FCSTD DOCUMENT  (FreeCAD 1.0R39319 (Git))
Label: caixa-chao
License: All rights reserved
LicenseURL: https://en.wikipedia.org/wiki/All_rights_reserved
objects: Part::Feature×1, Sketcher::SketchObject×1, PartDesign::Body×1
note: 4 computed .brp shape members not serialized (recipe doc carries the construction recipe); baked Part::Feature solids carry a one-line shape summary decoded from their .brp

FEATURE [Part::Feature] path46
  shape: bbox 266.2 x 266.2 x 2e-07 mm, 0 faces, 0 solids (baked)
FEATURE [Sketcher::SketchObject] Sketch
  ArcFitTolerance = 1e-06
  AttachmentSupport = -> [XY_Plane]
  FullyConstrained = true
  MakeInternals = false
  MapMode = 5
  sketch-geometry (28):
    g0: Circle CenterX=8 CenterY=-27.81 CenterZ=0 NormalX=0 NormalY=0 NormalZ=1 AngleXU=0 Radius=2
    g1: Circle CenterX=100.71 CenterY=-27.81 CenterZ=0 NormalX=0 NormalY=0 NormalZ=1 AngleXU=0 Radius=2
    g2: Circle CenterX=100.71 CenterY=-121.79 CenterZ=0 NormalX=0 NormalY=0 NormalZ=1 AngleXU=0 Radius=2
    g3: Circle CenterX=8 CenterY=-78.61 CenterZ=0 NormalX=0 NormalY=0 NormalZ=1 AngleXU=0 Radius=2
    g4: Circle CenterX=100.71 CenterY=-149.41 CenterZ=0 NormalX=0 NormalY=0 NormalZ=1 AngleXU=0 Radius=2
    g5: Circle CenterX=100.71 CenterY=-243.39 CenterZ=0 NormalX=0 NormalY=0 NormalZ=1 AngleXU=0 Radius=2
    g6: Circle CenterX=8 CenterY=-149.41 CenterZ=0 NormalX=0 NormalY=0 NormalZ=1 AngleXU=0 Radius=2
    g7: Circle CenterX=8 CenterY=-200.21 CenterZ=0 NormalX=0 NormalY=0 NormalZ=1 AngleXU=0 Radius=2
    g8: Circle CenterX=150.71 CenterY=-27.81 CenterZ=0 NormalX=0 NormalY=0 NormalZ=1 AngleXU=0 Radius=2
    g9: Circle CenterX=189.21 CenterY=-27.81 CenterZ=0 NormalX=0 NormalY=0 NormalZ=1 AngleXU=0 Radius=2
    g10: Circle CenterX=150.71 CenterY=-48.41 CenterZ=0 NormalX=0 NormalY=0 NormalZ=1 AngleXU=0 Radius=2
    g11: Circle CenterX=189.21 CenterY=-48.41 CenterZ=0 NormalX=0 NormalY=0 NormalZ=1 AngleXU=0 Radius=2
    g12: Circle CenterX=150.71 CenterY=-68.41 CenterZ=0 NormalX=0 NormalY=0 NormalZ=1 AngleXU=0 Radius=2
    g13: Circle CenterX=189.21 CenterY=-68.41 CenterZ=0 NormalX=0 NormalY=0 NormalZ=1 AngleXU=0 Radius=2
    g14: Circle CenterX=189.21 CenterY=-89.01 CenterZ=0 NormalX=0 NormalY=0 NormalZ=1 AngleXU=0 Radius=2
    g15: Circle CenterX=150.71 CenterY=-89.01 CenterZ=0 NormalX=0 NormalY=0 NormalZ=1 AngleXU=0 Radius=2
    g16: Circle CenterX=150.71 CenterY=-182.19 CenterZ=0 NormalX=0 NormalY=0 NormalZ=1 AngleXU=0 Radius=2
    g17: Circle CenterX=189.21 CenterY=-182.19 CenterZ=0 NormalX=0 NormalY=0 NormalZ=1 AngleXU=0 Radius=2
    g18: Circle CenterX=150.71 CenterY=-202.79 CenterZ=0 NormalX=0 NormalY=0 NormalZ=1 AngleXU=0 Radius=2
    g19: Circle CenterX=189.21 CenterY=-202.79 CenterZ=0 NormalX=0 NormalY=0 NormalZ=1 AngleXU=0 Radius=2
    g20: Circle CenterX=150.71 CenterY=-222.79 CenterZ=0 NormalX=0 NormalY=0 NormalZ=1 AngleXU=0 Radius=2
    g21: Circle CenterX=189.21 CenterY=-222.79 CenterZ=0 NormalX=0 NormalY=0 NormalZ=1 AngleXU=0 Radius=2
    g22: Circle CenterX=150.71 CenterY=-243.39 CenterZ=0 NormalX=0 NormalY=0 NormalZ=1 AngleXU=0 Radius=2
    g23: Circle CenterX=189.21 CenterY=-243.39 CenterZ=0 NormalX=0 NormalY=0 NormalZ=1 AngleXU=0 Radius=2
    g24: Circle CenterX=164 CenterY=-114.2 CenterZ=0 NormalX=0 NormalY=0 NormalZ=1 AngleXU=0 Radius=2
    g25: Circle CenterX=252 CenterY=-114.2 CenterZ=0 NormalX=0 NormalY=0 NormalZ=1 AngleXU=0 Radius=2
    g26: Circle CenterX=164 CenterY=-152.2 CenterZ=0 NormalX=0 NormalY=0 NormalZ=1 AngleXU=0 Radius=2
    g27: Circle CenterX=252 CenterY=-152.2 CenterZ=0 NormalX=0 NormalY=0 NormalZ=1 AngleXU=0 Radius=2
  constraints (84):
    c: Diameter(g0) = 4
    c: DistanceX(g-1,g0) = 8
    c: DistanceY(g0,g-1) = 27.81
    c: Equal(g1,g0)
    c: Horizontal(g0,g1)
    c: DistanceX(g0,g1) = 92.71
    c: Vertical(g2,g1)
    c: DistanceY(g2,g1) = 93.98
    c: DistanceY(g3,g0) = 50.8
    c: Equal(g3,g0)
    c: Vertical(g0,g3)
    c: Equal(g1,g2)
    c: Equal(g4,g2)
    c: Vertical(g4,g2)
    c: DistanceY(g4,g2) = 27.62
    c: DistanceY(g5,g4) = 93.98
    c: Horizontal(g6,g4)
    c: Vertical(g7,g6)
    c: Equal(g6,g7)
    c: Equal(g7,g5)
    c: Equal(g5,g4)
    c: DistanceX(g6,g4) = 92.71
    c: Vertical(g5,g4)
    c: DistanceY(g7,g6) = 50.8
    c: Equal(g8,g9)
    c: Equal(g9,g11)
    c: Equal(g11,g10)
    c: Equal(g1,g8)
    c: Horizontal(g8,g9)
    c: Horizontal(g10,g11)
    c: Vertical(g10,g8)
    c: Vertical(g11,g9)
    c: DistanceY(g11,g9) = 20.6
    c: DistanceX(g10,g11) = 38.5
    c: Horizontal(g1,g8)
    c: DistanceX(g1,g8) = 50
    c: Equal(g15,g14)
    c: Equal(g14,g13)
    c: Equal(g13,g12)
    c: Equal(g12,g10)
    c: Vertical(g12,g15)
    c: Vertical(g14,g13)
    c: Horizontal(g12,g13)
    c: Horizontal(g14,g15)
    c: DistanceY(g14,g13) = 20.6
    c: DistanceX(g12,g13) = 38.5
    c: DistanceY(g12,g10) = 20
    c: Vertical(g12,g10)
    c: Vertical(g23,g21)
    c: Vertical(g21,g19)
    c: Vertical(g19,g17)
    c: Horizontal(g16,g17)
    c: Horizontal(g18,g19)
    c: Horizontal(g20,g21)
    c: Horizontal(g22,g23)
    c: Equal(g22,g23)
    c: Equal(g23,g21)
    c: Equal(g21,g20)
    c: Equal(g20,g18)
    c: Equal(g18,g19)
    c: Equal(g19,g17)
    c: Equal(g17,g16)
    c: Equal(g16,g15)
    c: Vertical(g22,g20)
    c: Vertical(g20,g18)
    c: Vertical(g18,g16)
    c: Vertical(g16,g15)
    c: Vertical(g17,g14)
    c: DistanceY(g19,g17) = 20.6
    c: DistanceY(g21,g19) = 20
    c: DistanceY(g23,g21) = 20.6
    c: Horizontal(g5,g22)
    c: Horizontal(g26,g27)
    c: Horizontal(g25,g24)
    c: Vertical(g24,g26)
    c: Vertical(g27,g25)
    c: Equal(g26,g24)
    c: Equal(g24,g25)
    c: Equal(g25,g27)
    c: Equal(g27,g17)
    c: DistanceX(g24,g25) = 88
    c: DistanceY(g27,g25) = 38
    c: DistanceY(g25,g-1) = 114.2
    c: DistanceX(g-1,g25) = 252
FEATURE [PartDesign::Body] Body
  AllowCompound = false
  Group = -> [Sketch]
  Origin = -> Origin
